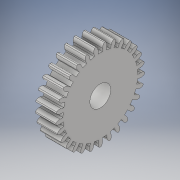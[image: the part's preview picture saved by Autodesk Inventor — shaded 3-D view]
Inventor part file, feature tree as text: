
AUTODESK INVENTOR PART (.ipt)
format: ipt  version: 2018 (Build 220112000, 112)  size: 483,840 bytes
history: native  units: in
note: dims shown in document units (in); Inventor stores cm internally (conversion verified against a paired STEP export)
features: extrude x3, sketch x3
ambient origin geometry x8: Origin, YZ Plane, XZ Plane, XY Plane, X Axis, Y Axis, Z Axis, Center Point
bodies: Body1 (feature_tree)
feature tree (6):
  extrude  "Extrusion6"  Depth=0.196in
  extrude  "Extrusion7"  Depth=0.2756in TaperAngle=0.0deg
  extrude  "Extrusion8"  Depth=0.2756in TaperAngle=0.0deg
  sketch  "Sketch1"  dims[d0=1.0in d16=0.196in]
  sketch  "Sketch2"  dims[d35=11.4173in d37=360.0deg d39=0.2756in d40=0.0in]
  sketch  "Sketch3"  dims[d41=0.25in d42=0.2756in d43=0.0in d44=0.28in d45=0.3937in d46=0.0in]
